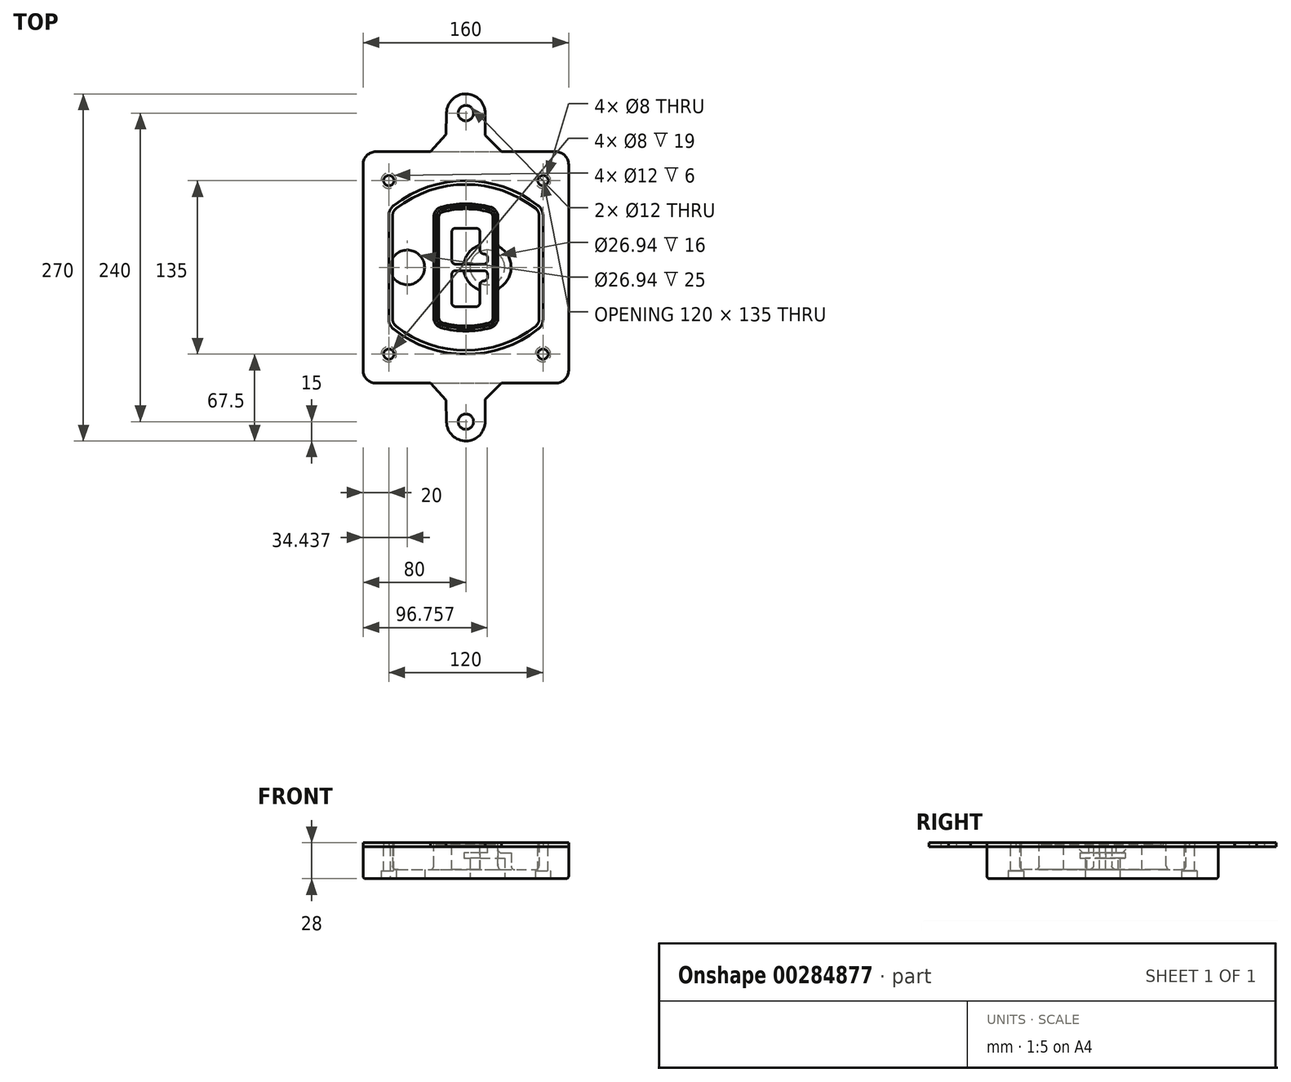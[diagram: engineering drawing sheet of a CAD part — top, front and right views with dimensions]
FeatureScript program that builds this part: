
annotation { "Feature Type Name" : "Feature", "Feature Type Description" : "" }
export const myFeature = defineFeature(function(context is Context, id is Id, definition is map)
    precondition{}
    {
        {
            var Q0;
            Q0=qCreatedBy(makeId("Top.planeOp"),FACE);
            var sketch = newSketch(context, id + "F0", { "sketchPlane" : qUnion([Q0])});
            skPoint(sketch, "E0.rect.middle", {"position": v(0, 0) * mm});
            skLineSegment(sketch, "E1.bottom", {"start": v(-70, -90) * mm, "end": v(70, -90) * mm});
            skLineSegment(sketch, "E1.top", {"start": v(-70, 90) * mm, "end": v(70, 90) * mm});
            skLineSegment(sketch, "E1.left", {"start": v(-80, -80) * mm, "end": v(-80, 80) * mm});
            skLineSegment(sketch, "E1.right", {"start": v(80, -80) * mm, "end": v(80, 80) * mm});
            skLineSegment(sketch, "E2", {"start": v(-80, 90) * mm, "end": v(80, -90) * mm, "construction": true});
            skLineSegment(sketch, "E3", {"start": v(80, 90) * mm, "end": v(-80, -90) * mm, "construction": true});
            skCircle(sketch, "E4", {"center": v(-60, 67.5) * mm, "radius": 4 * mm});
            skCircle(sketch, "E5", {"center": v(60, 67.5) * mm, "radius": 4 * mm});
            skCircle(sketch, "E6", {"center": v(60, -67.5) * mm, "radius": 4 * mm});
            skCircle(sketch, "E7", {"center": v(-60, -67.5) * mm, "radius": 4 * mm});
            skLineSegment(sketch, "E8", {"start": v(-60, 67.5) * mm, "end": v(60, 67.5) * mm, "construction": true});
            skLineSegment(sketch, "E9", {"start": v(60, 67.5) * mm, "end": v(60, -67.5) * mm, "construction": true});
            skLineSegment(sketch, "E10", {"start": v(60, -67.5) * mm, "end": v(-60, -67.5) * mm, "construction": true});
            skLineSegment(sketch, "E11", {"start": v(-60, -67.5) * mm, "end": v(-60, 67.5) * mm, "construction": true});
            skLineSegment(sketch, "E12", {"start": v(-60, 40.3) * mm, "end": v(-60, -40.3) * mm});
            skLineSegment(sketch, "E13", {"start": v(60, 40.3) * mm, "end": v(60, -40.3) * mm});
            skArc(sketch, "E14", {"start": v(56.15, 48.18) * mm, "mid": v(0, 67.5) * mm, "end": v(-56.15, 48.18) * mm});
            skArc(sketch, "E15", {"start": v(-56.15, -48.18) * mm, "mid": v(0, -67.5) * mm, "end": v(56.15, -48.18) * mm});
            skLineSegment(sketch, "E16", {"start": v(-60, 0) * mm, "end": v(60, 0) * mm, "construction": true});
            skPoint(sketch, "E17.visualSharp", {"position": v(-60, -45) * mm});
            skArc(sketch, "E17.filletArc", {"start": v(-60, -40.3) * mm, "mid": v(-58.99, -44.68) * mm, "end": v(-56.15, -48.18) * mm});
            skPoint(sketch, "E18.visualSharp", {"position": v(-60, 45) * mm});
            skArc(sketch, "E18.filletArc", {"start": v(-56.15, 48.18) * mm, "mid": v(-58.99, 44.68) * mm, "end": v(-60, 40.3) * mm});
            skPoint(sketch, "E19.visualSharp", {"position": v(60, 45) * mm});
            skArc(sketch, "E19.filletArc", {"start": v(60, 40.3) * mm, "mid": v(58.99, 44.68) * mm, "end": v(56.15, 48.18) * mm});
            skPoint(sketch, "E20.visualSharp", {"position": v(60, -45) * mm});
            skArc(sketch, "E20.filletArc", {"start": v(56.15, -48.18) * mm, "mid": v(58.99, -44.68) * mm, "end": v(60, -40.3) * mm});
            skPoint(sketch, "E21.visualSharp", {"position": v(-80, 90) * mm});
            skArc(sketch, "E21.filletArc", {"start": v(-70, 90) * mm, "mid": v(-77.07, 87.07) * mm, "end": v(-80, 80) * mm});
            skPoint(sketch, "E22.visualSharp", {"position": v(80, 90) * mm});
            skArc(sketch, "E22.filletArc", {"start": v(80, 80) * mm, "mid": v(77.07, 87.07) * mm, "end": v(70, 90) * mm});
            skPoint(sketch, "E23.visualSharp", {"position": v(80, -90) * mm});
            skArc(sketch, "E23.filletArc", {"start": v(70, -90) * mm, "mid": v(77.07, -87.07) * mm, "end": v(80, -80) * mm});
            skPoint(sketch, "E24.visualSharp", {"position": v(-80, -90) * mm});
            skArc(sketch, "E24.filletArc", {"start": v(-80, -80) * mm, "mid": v(-77.07, -87.07) * mm, "end": v(-70, -90) * mm});
            skArc(sketch, "E25.0", {"start": v(57, 40.3) * mm, "mid": v(56.3, 43.36) * mm, "end": v(54.3, 45.81) * mm});
            skLineSegment(sketch, "E25.1", {"start": v(57, 40.3) * mm, "end": v(57, -40.3) * mm});
            skArc(sketch, "E25.2", {"start": v(54.3, -45.81) * mm, "mid": v(56.3, -43.36) * mm, "end": v(57, -40.3) * mm});
            skArc(sketch, "E25.3", {"start": v(-54.3, -45.81) * mm, "mid": v(0, -64.5) * mm, "end": v(54.3, -45.81) * mm});
            skArc(sketch, "E25.4", {"start": v(-57, -40.3) * mm, "mid": v(-56.3, -43.36) * mm, "end": v(-54.3, -45.81) * mm});
            skArc(sketch, "E25.5", {"start": v(54.3, 45.81) * mm, "mid": v(0, 64.5) * mm, "end": v(-54.3, 45.81) * mm});
            skLineSegment(sketch, "E25.6", {"start": v(-57, 40.3) * mm, "end": v(-57, -40.3) * mm});
            skArc(sketch, "E25.7", {"start": v(-54.3, 45.81) * mm, "mid": v(-56.3, 43.36) * mm, "end": v(-57, 40.3) * mm});
            skArc(sketch, "E26.0", {"start": v(-58.62, 51.33) * mm, "mid": v(-62.58, 46.43) * mm, "end": v(-64, 40.3) * mm});
            skArc(sketch, "E26.1", {"start": v(58.62, 51.33) * mm, "mid": v(0, 71.5) * mm, "end": v(-58.62, 51.33) * mm});
            skArc(sketch, "E26.2", {"start": v(64, 40.3) * mm, "mid": v(62.58, 46.43) * mm, "end": v(58.62, 51.33) * mm});
            skLineSegment(sketch, "E26.3", {"start": v(64, 40.3) * mm, "end": v(64, -40.3) * mm});
            skArc(sketch, "E26.4", {"start": v(58.62, -51.33) * mm, "mid": v(62.58, -46.43) * mm, "end": v(64, -40.3) * mm});
            skLineSegment(sketch, "E26.5", {"start": v(-64, 40.3) * mm, "end": v(-64, -40.3) * mm});
            skArc(sketch, "E26.6", {"start": v(-58.62, -51.33) * mm, "mid": v(0, -71.5) * mm, "end": v(58.62, -51.33) * mm});
            skArc(sketch, "E26.7", {"start": v(-64, -40.3) * mm, "mid": v(-62.58, -46.43) * mm, "end": v(-58.62, -51.33) * mm});
            skSolve(sketch);
        }
        {
            var Q0;
            Q0=makeQuery(id+"F0.imprint","IMPRINT",FACE,{"disambiguationData":[TD([[makeQuery(id+"F0.imprint","IMPRINT",EDGE,{"derivedFrom":sQuery(id+"F0.wireOp",EDGE,"E1.bottom")}),1.0]])]});
            var Q1;
            Q1=makeQuery(id+"F0.imprint","IMPRINT",FACE,{"disambiguationData":[TD([[makeQuery(id+"F0.imprint","IMPRINT",EDGE,{"derivedFrom":sQuery(id+"F0.wireOp",EDGE,"E12")}),1.0]])]});
            var Q2;
            Q2=makeQuery(id+"F0.imprint","IMPRINT",FACE,{"disambiguationData":[TD([[makeQuery(id+"F0.imprint","IMPRINT",EDGE,{"derivedFrom":sQuery(id+"F0.wireOp",EDGE,"E25.0")}),1.0]])]});
            var Q3;
            Q3=makeQuery(id+"F0.imprint","IMPRINT",FACE,{"disambiguationData":[TD([[makeQuery(id+"F0.imprint","IMPRINT",EDGE,{"derivedFrom":sQuery(id+"F0.wireOp",EDGE,"E12")}),-1.0]])]});
            extrude(context, id + "F1", {"entities" : qUnion([Q0, Q1, Q2, Q3]), "oppositeDirection" : true, "depth" : 25 * mm});
        }
        {
            var Q0;
            Q0=makeQuery(id+"F0.imprint","IMPRINT",FACE,{"disambiguationData":[TD([[makeQuery(id+"F0.imprint","IMPRINT",EDGE,{"derivedFrom":sQuery(id+"F0.wireOp",EDGE,"E12")}),1.0]])]});
            extrude(context, id + "F2", {"entities" : qUnion([Q0]), "operationType" : NewBodyOperationType.ADD, "depth" : 3 * mm});
        }
        {
            var Q0;
            Q0=makeQuery(id+"F0.imprint","IMPRINT",FACE,{"disambiguationData":[TD([[makeQuery(id+"F0.imprint","IMPRINT",EDGE,{"derivedFrom":sQuery(id+"F0.wireOp",EDGE,"E25.0")}),1.0]])]});
            extrude(context, id + "F3", {"entities" : qUnion([Q0]), "operationType" : NewBodyOperationType.REMOVE, "oppositeDirection" : true, "depth" : 18 * mm});
        }
        {
            var Q0;
            Q0=makeQuery(id+"F2.opExtrude","CAP_FACE",FACE,{"disambiguationData":[OSD([sQuery(id+"F0.wireOp",EDGE,"E12"),sQuery(id+"F0.wireOp",EDGE,"E13"),sQuery(id+"F0.wireOp",EDGE,"E14"),sQuery(id+"F0.wireOp",EDGE,"E15"),sQuery(id+"F0.wireOp",EDGE,"E17.filletArc"),sQuery(id+"F0.wireOp",EDGE,"E18.filletArc"),sQuery(id+"F0.wireOp",EDGE,"E19.filletArc"),sQuery(id+"F0.wireOp",EDGE,"E20.filletArc"),sQuery(id+"F0.wireOp",EDGE,"E25.0"),sQuery(id+"F0.wireOp",EDGE,"E25.1"),sQuery(id+"F0.wireOp",EDGE,"E25.2"),sQuery(id+"F0.wireOp",EDGE,"E25.3"),sQuery(id+"F0.wireOp",EDGE,"E25.4"),sQuery(id+"F0.wireOp",EDGE,"E25.5"),sQuery(id+"F0.wireOp",EDGE,"E25.6"),sQuery(id+"F0.wireOp",EDGE,"E25.7")])],"isStart":false});
            var sketch = newSketch(context, id + "F4", { "sketchPlane" : qUnion([Q0])});
            skArc(sketch, "E27.0", {"start": v(-19.08, -46.97) * mm, "mid": v(0, -49.5) * mm, "end": v(19.08, -46.97) * mm});
            skArc(sketch, "E28.0", {"start": v(19.08, 46.97) * mm, "mid": v(0, 49.5) * mm, "end": v(-19.08, 46.97) * mm});
            skLineSegment(sketch, "E29", {"start": v(-25, 39.25) * mm, "end": v(-25, -39.25) * mm});
            skLineSegment(sketch, "E30", {"start": v(25, 39.25) * mm, "end": v(25, -39.25) * mm});
            skLineSegment(sketch, "E31", {"start": v(-25, 45.1) * mm, "end": v(25, 45.1) * mm, "construction": true});
            skLineSegment(sketch, "E32", {"start": v(-25, -45.1) * mm, "end": v(25, -45.1) * mm, "construction": true});
            skPoint(sketch, "E33.visualSharp", {"position": v(-25, 45.1) * mm});
            skArc(sketch, "E33.filletArc", {"start": v(-19.08, 46.97) * mm, "mid": v(-23.35, 44.11) * mm, "end": v(-25, 39.25) * mm});
            skPoint(sketch, "E34.visualSharp", {"position": v(25, 45.1) * mm});
            skArc(sketch, "E34.filletArc", {"start": v(25, 39.25) * mm, "mid": v(23.35, 44.11) * mm, "end": v(19.08, 46.97) * mm});
            skPoint(sketch, "E35.visualSharp", {"position": v(25, -45.1) * mm});
            skArc(sketch, "E35.filletArc", {"start": v(19.08, -46.97) * mm, "mid": v(23.35, -44.11) * mm, "end": v(25, -39.25) * mm});
            skPoint(sketch, "E36.visualSharp", {"position": v(-25, -45.1) * mm});
            skArc(sketch, "E36.filletArc", {"start": v(-25, -39.25) * mm, "mid": v(-23.35, -44.11) * mm, "end": v(-19.08, -46.97) * mm});
            skArc(sketch, "E37.0", {"start": v(54.3, 45.81) * mm, "mid": v(0, 64.5) * mm, "end": v(-54.3, 45.81) * mm});
            skArc(sketch, "E37.1", {"start": v(-54.3, 45.81) * mm, "mid": v(-56.3, 43.36) * mm, "end": v(-57, 40.3) * mm});
            skLineSegment(sketch, "E37.2", {"start": v(-57, 40.3) * mm, "end": v(-57, -40.3) * mm});
            skArc(sketch, "E37.3", {"start": v(-57, -40.3) * mm, "mid": v(-56.3, -43.36) * mm, "end": v(-54.3, -45.81) * mm});
            skArc(sketch, "E37.4", {"start": v(-54.3, -45.81) * mm, "mid": v(0, -64.5) * mm, "end": v(54.3, -45.81) * mm});
            skArc(sketch, "E37.5", {"start": v(54.3, -45.81) * mm, "mid": v(56.3, -43.36) * mm, "end": v(57, -40.3) * mm});
            skLineSegment(sketch, "E37.6", {"start": v(57, 40.3) * mm, "end": v(57, -40.3) * mm});
            skArc(sketch, "E37.7", {"start": v(57, 40.3) * mm, "mid": v(56.3, 43.36) * mm, "end": v(54.3, 45.81) * mm});
            skLineSegment(sketch, "E38.0", {"start": v(23, 39.25) * mm, "end": v(23, -39.25) * mm});
            skArc(sketch, "E38.1", {"start": v(18.56, -45.04) * mm, "mid": v(21.76, -42.9) * mm, "end": v(23, -39.25) * mm});
            skArc(sketch, "E38.2", {"start": v(-18.56, -45.04) * mm, "mid": v(0, -47.5) * mm, "end": v(18.56, -45.04) * mm});
            skArc(sketch, "E38.3", {"start": v(-23, -39.25) * mm, "mid": v(-21.76, -42.9) * mm, "end": v(-18.56, -45.04) * mm});
            skLineSegment(sketch, "E38.4", {"start": v(-23, 39.25) * mm, "end": v(-23, -39.25) * mm});
            skArc(sketch, "E38.5", {"start": v(23, 39.25) * mm, "mid": v(21.76, 42.9) * mm, "end": v(18.56, 45.04) * mm});
            skArc(sketch, "E38.6", {"start": v(-18.56, 45.04) * mm, "mid": v(-21.76, 42.9) * mm, "end": v(-23, 39.25) * mm});
            skArc(sketch, "E38.7", {"start": v(18.56, 45.04) * mm, "mid": v(0, 47.5) * mm, "end": v(-18.56, 45.04) * mm});
            skArc(sketch, "E39.0", {"start": v(21, 39.25) * mm, "mid": v(20.18, 41.68) * mm, "end": v(18.04, 43.1) * mm});
            skLineSegment(sketch, "E39.1", {"start": v(21, 39.25) * mm, "end": v(21, -39.25) * mm});
            skArc(sketch, "E39.2", {"start": v(18.04, -43.1) * mm, "mid": v(20.18, -41.68) * mm, "end": v(21, -39.25) * mm});
            skArc(sketch, "E39.3", {"start": v(-18.04, -43.1) * mm, "mid": v(0, -45.5) * mm, "end": v(18.04, -43.1) * mm});
            skArc(sketch, "E39.4", {"start": v(-21, -39.25) * mm, "mid": v(-20.18, -41.68) * mm, "end": v(-18.04, -43.1) * mm});
            skArc(sketch, "E39.5", {"start": v(18.04, 43.1) * mm, "mid": v(0, 45.5) * mm, "end": v(-18.04, 43.1) * mm});
            skLineSegment(sketch, "E39.6", {"start": v(-21, 39.25) * mm, "end": v(-21, -39.25) * mm});
            skArc(sketch, "E39.7", {"start": v(-18.04, 43.1) * mm, "mid": v(-20.18, 41.68) * mm, "end": v(-21, 39.25) * mm});
            skLineSegment(sketch, "E40", {"start": v(-25, 0) * mm, "end": v(25, 0) * mm, "construction": true});
            skLineSegment(sketch, "E41", {"start": v(-11, 5.5) * mm, "end": v(-11, 27.5) * mm});
            skLineSegment(sketch, "E42", {"start": v(-8, 30.5) * mm, "end": v(8, 30.5) * mm});
            skLineSegment(sketch, "E43", {"start": v(11, 27.5) * mm, "end": v(11, 13.5) * mm});
            skLineSegment(sketch, "E44", {"start": v(14, 10.5) * mm, "end": v(14, 10.5) * mm});
            skLineSegment(sketch, "E45", {"start": v(17, 7.5) * mm, "end": v(17, 5.5) * mm});
            skLineSegment(sketch, "E46", {"start": v(14, 2.5) * mm, "end": v(-8, 2.5) * mm});
            skPoint(sketch, "E47.visualSharp", {"position": v(-11, 30.5) * mm});
            skArc(sketch, "E47.filletArc", {"start": v(-8, 30.5) * mm, "mid": v(-10.12, 29.62) * mm, "end": v(-11, 27.5) * mm});
            skPoint(sketch, "E48.visualSharp", {"position": v(11, 30.5) * mm});
            skArc(sketch, "E48.filletArc", {"start": v(11, 27.5) * mm, "mid": v(10.12, 29.62) * mm, "end": v(8, 30.5) * mm});
            skPoint(sketch, "E49.visualSharp", {"position": v(11, 10.5) * mm});
            skArc(sketch, "E49.filletArc", {"start": v(11, 13.5) * mm, "mid": v(11.88, 11.38) * mm, "end": v(14, 10.5) * mm});
            skPoint(sketch, "E50.visualSharp", {"position": v(17, 10.5) * mm});
            skArc(sketch, "E50.filletArc", {"start": v(17, 7.5) * mm, "mid": v(16.12, 9.62) * mm, "end": v(14, 10.5) * mm});
            skPoint(sketch, "E51.visualSharp", {"position": v(17, 2.5) * mm});
            skArc(sketch, "E51.filletArc", {"start": v(14, 2.5) * mm, "mid": v(16.12, 3.38) * mm, "end": v(17, 5.5) * mm});
            skPoint(sketch, "E52.visualSharp", {"position": v(-11, 2.5) * mm});
            skArc(sketch, "E52.filletArc", {"start": v(-11, 5.5) * mm, "mid": v(-10.12, 3.38) * mm, "end": v(-8, 2.5) * mm});
            skLineSegment(sketch, "E53.0.MirrorCS", {"start": v(14, -2.5) * mm, "end": v(-8, -2.5) * mm});
            skArc(sketch, "E54.0.MirrorCS", {"start": v(-11, -5.5) * mm, "mid": v(-10.12, -3.38) * mm, "end": v(-8, -2.5) * mm});
            skLineSegment(sketch, "E55.0.MirrorCS", {"start": v(-11, -5.5) * mm, "end": v(-11, -27.5) * mm});
            skArc(sketch, "E56.0.MirrorCS", {"start": v(-8, -30.5) * mm, "mid": v(-10.12, -29.62) * mm, "end": v(-11, -27.5) * mm});
            skLineSegment(sketch, "E57.0.MirrorCS", {"start": v(-8, -30.5) * mm, "end": v(8, -30.5) * mm});
            skArc(sketch, "E58.0.MirrorCS", {"start": v(11, -27.5) * mm, "mid": v(10.12, -29.62) * mm, "end": v(8, -30.5) * mm});
            skLineSegment(sketch, "E59.0.MirrorCS", {"start": v(11, -27.5) * mm, "end": v(11, -13.5) * mm});
            skArc(sketch, "E60.0.MirrorCS", {"start": v(11, -13.5) * mm, "mid": v(11.88, -11.38) * mm, "end": v(14, -10.5) * mm});
            skArc(sketch, "E61.0.MirrorCS", {"start": v(17, -7.5) * mm, "mid": v(16.12, -9.62) * mm, "end": v(14, -10.5) * mm});
            skLineSegment(sketch, "E62.0.MirrorCS", {"start": v(17, -7.5) * mm, "end": v(17, -5.5) * mm});
            skArc(sketch, "E63.0.MirrorCS", {"start": v(14, -2.5) * mm, "mid": v(16.12, -3.38) * mm, "end": v(17, -5.5) * mm});
            skSolve(sketch);
        }
        {
            var Q0;
            Q0=makeQuery(id+"F4.imprint","IMPRINT",FACE,{"disambiguationData":[TD([[makeQuery(id+"F4.imprint","IMPRINT",EDGE,{"derivedFrom":sQuery(id+"F4.wireOp",EDGE,"E27.0")}),1.0]])]});
            var Q1;
            Q1=makeQuery(id+"F4.imprint","IMPRINT",FACE,{"disambiguationData":[TD([[makeQuery(id+"F4.imprint","IMPRINT",EDGE,{"derivedFrom":sQuery(id+"F4.wireOp",EDGE,"E38.0")}),-1.0]])]});
            var Q2;
            Q2=makeQuery(id+"F4.imprint","IMPRINT",FACE,{"disambiguationData":[TD([[makeQuery(id+"F4.imprint","IMPRINT",EDGE,{"derivedFrom":sQuery(id+"F4.wireOp",EDGE,"E39.0")}),1.0]])]});
            extrude(context, id + "F5", {"entities" : qUnion([Q0, Q1, Q2]), "operationType" : NewBodyOperationType.ADD, "endBound" : BoundingType.UP_TO_NEXT, "oppositeDirection" : true, "depth" : 25 * mm});
        }
        {
            var Q0;
            Q0=makeQuery(id+"F4.imprint","IMPRINT",FACE,{"disambiguationData":[TD([[makeQuery(id+"F4.imprint","IMPRINT",EDGE,{"derivedFrom":sQuery(id+"F4.wireOp",EDGE,"E38.0")}),-1.0]])]});
            extrude(context, id + "F6", {"entities" : qUnion([Q0]), "operationType" : NewBodyOperationType.REMOVE, "oppositeDirection" : true, "depth" : 2 * mm});
        }
        {
            var Q0;
            Q0=makeQuery(id+"F1.opExtrude","CAP_FACE",FACE,{"disambiguationData":[OSD([sQuery(id+"F0.wireOp",EDGE,"E1.bottom"),sQuery(id+"F0.wireOp",EDGE,"E1.top"),sQuery(id+"F0.wireOp",EDGE,"E1.left"),sQuery(id+"F0.wireOp",EDGE,"E1.right"),sQuery(id+"F0.wireOp",EDGE,"E4"),sQuery(id+"F0.wireOp",EDGE,"E5"),sQuery(id+"F0.wireOp",EDGE,"E6"),sQuery(id+"F0.wireOp",EDGE,"E7"),sQuery(id+"F0.wireOp",EDGE,"E21.filletArc"),sQuery(id+"F0.wireOp",EDGE,"E22.filletArc"),sQuery(id+"F0.wireOp",EDGE,"E23.filletArc"),sQuery(id+"F0.wireOp",EDGE,"E24.filletArc")])],"isStart":false});
            var sketch = newSketch(context, id + "F7", { "sketchPlane" : qUnion([Q0])});
            skCircle(sketch, "E64", {"center": v(16.76, 0) * mm, "radius": 13.47 * mm});
            skCircle(sketch, "E65", {"center": v(-45.56, 0) * mm, "radius": 13.47 * mm});
            skLineSegment(sketch, "E66", {"start": v(80, 0) * mm, "end": v(-80, 0) * mm});
            skCircle(sketch, "E67", {"center": v(16.76, 0) * mm, "radius": 18.47 * mm});
            skCircle(sketch, "E68", {"center": v(60, -67.5) * mm, "radius": 6 * mm});
            skCircle(sketch, "E69", {"center": v(-60, -67.5) * mm, "radius": 6 * mm});
            skCircle(sketch, "E70", {"center": v(-60, 67.5) * mm, "radius": 6 * mm});
            skCircle(sketch, "E71", {"center": v(60, 67.5) * mm, "radius": 6 * mm});
            skSolve(sketch);
        }
        {
            var Q0;
            {var subQ1=sQuery(id+"F7.wireOp",EDGE,"E66");var subQ4=sQuery(id+"F7.wireOp",EDGE,"E64");var subQ6=makeQuery(id+"F7.imprint","INTERSECT",VERTEX,{"disambiguationData":[OD(0.0)],"derivedFrom":[subQ4,subQ1]});Q0=makeQuery(id+"F7.imprint","IMPRINT",FACE,{"disambiguationData":[TD([[makeQuery(id+"F7.imprint","IMPRINT",EDGE,{"disambiguationData":[TD([[subQ6,-1.0]])],"derivedFrom":subQ4}),-1.0]])]});}
            var Q1;
            {var subQ0=sQuery(id+"F7.wireOp",EDGE,"E66");var subQ1=sQuery(id+"F7.wireOp",EDGE,"E64");var subQ3=makeQuery(id+"F7.imprint","INTERSECT",VERTEX,{"disambiguationData":[OD(0.0)],"derivedFrom":[subQ1,subQ0]});Q1=makeQuery(id+"F7.imprint","IMPRINT",FACE,{"disambiguationData":[TD([[makeQuery(id+"F7.imprint","IMPRINT",EDGE,{"disambiguationData":[TD([[subQ3,-1.0]])],"derivedFrom":subQ1}),1.0]])]});}
            var Q2;
            {var subQ0=sQuery(id+"F7.wireOp",EDGE,"E66");var subQ1=sQuery(id+"F7.wireOp",EDGE,"E64");var subQ3=makeQuery(id+"F7.imprint","INTERSECT",VERTEX,{"disambiguationData":[OD(0.0)],"derivedFrom":[subQ1,subQ0]});Q2=makeQuery(id+"F7.imprint","IMPRINT",FACE,{"disambiguationData":[TD([[makeQuery(id+"F7.imprint","IMPRINT",EDGE,{"disambiguationData":[TD([[subQ3,1.0]])],"derivedFrom":subQ1}),1.0]])]});}
            var Q3;
            {var subQ1=sQuery(id+"F7.wireOp",EDGE,"E66");var subQ4=sQuery(id+"F7.wireOp",EDGE,"E64");var subQ6=makeQuery(id+"F7.imprint","INTERSECT",VERTEX,{"disambiguationData":[OD(0.0)],"derivedFrom":[subQ4,subQ1]});Q3=makeQuery(id+"F7.imprint","IMPRINT",FACE,{"disambiguationData":[TD([[makeQuery(id+"F7.imprint","IMPRINT",EDGE,{"disambiguationData":[TD([[subQ6,1.0]])],"derivedFrom":subQ4}),-1.0]])]});}
            extrude(context, id + "F8", {"entities" : qUnion([Q0, Q1, Q2, Q3]), "operationType" : NewBodyOperationType.ADD, "oppositeDirection" : true, "depth" : 20 * mm});
        }
        {
            var Q0;
            {var subQ0=sQuery(id+"F7.wireOp",EDGE,"E66");var subQ1=sQuery(id+"F7.wireOp",EDGE,"E64");var subQ3=makeQuery(id+"F7.imprint","INTERSECT",VERTEX,{"disambiguationData":[OD(0.0)],"derivedFrom":[subQ1,subQ0]});Q0=makeQuery(id+"F7.imprint","IMPRINT",FACE,{"disambiguationData":[TD([[makeQuery(id+"F7.imprint","IMPRINT",EDGE,{"disambiguationData":[TD([[subQ3,-1.0]])],"derivedFrom":subQ1}),1.0]])]});}
            var Q1;
            {var subQ0=sQuery(id+"F7.wireOp",EDGE,"E66");var subQ1=sQuery(id+"F7.wireOp",EDGE,"E64");var subQ3=makeQuery(id+"F7.imprint","INTERSECT",VERTEX,{"disambiguationData":[OD(0.0)],"derivedFrom":[subQ1,subQ0]});Q1=makeQuery(id+"F7.imprint","IMPRINT",FACE,{"disambiguationData":[TD([[makeQuery(id+"F7.imprint","IMPRINT",EDGE,{"disambiguationData":[TD([[subQ3,1.0]])],"derivedFrom":subQ1}),1.0]])]});}
            extrude(context, id + "F9", {"entities" : qUnion([Q0, Q1]), "operationType" : NewBodyOperationType.REMOVE, "oppositeDirection" : true, "depth" : 16 * mm});
        }
        {
            var Q0;
            {var subQ0=sQuery(id+"F7.wireOp",EDGE,"E66");var subQ1=sQuery(id+"F7.wireOp",EDGE,"E65");var subQ3=makeQuery(id+"F7.imprint","INTERSECT",VERTEX,{"disambiguationData":[OD(0.0)],"derivedFrom":[subQ1,subQ0]});Q0=makeQuery(id+"F7.imprint","IMPRINT",FACE,{"disambiguationData":[TD([[makeQuery(id+"F7.imprint","IMPRINT",EDGE,{"disambiguationData":[TD([[subQ3,-1.0]])],"derivedFrom":subQ1}),1.0]])]});}
            var Q1;
            {var subQ0=sQuery(id+"F7.wireOp",EDGE,"E66");var subQ1=sQuery(id+"F7.wireOp",EDGE,"E65");var subQ3=makeQuery(id+"F7.imprint","INTERSECT",VERTEX,{"disambiguationData":[OD(0.0)],"derivedFrom":[subQ1,subQ0]});Q1=makeQuery(id+"F7.imprint","IMPRINT",FACE,{"disambiguationData":[TD([[makeQuery(id+"F7.imprint","IMPRINT",EDGE,{"disambiguationData":[TD([[subQ3,1.0]])],"derivedFrom":subQ1}),1.0]])]});}
            extrude(context, id + "F10", {"entities" : qUnion([Q0, Q1]), "operationType" : NewBodyOperationType.REMOVE, "oppositeDirection" : true, "depth" : 25 * mm});
        }
        {
            var Q0;
            Q0=makeQuery(id+"F7.imprint","IMPRINT",FACE,{"disambiguationData":[TD([[makeQuery(id+"F7.imprint","IMPRINT",EDGE,{"derivedFrom":sQuery(id+"F7.wireOp",EDGE,"E68")}),1.0]])]});
            var Q1;
            Q1=makeQuery(id+"F7.imprint","IMPRINT",FACE,{"disambiguationData":[TD([[makeQuery(id+"F7.imprint","IMPRINT",EDGE,{"derivedFrom":makeQuery(id+"F1.opExtrude","CAP_EDGE",EDGE,{"disambiguationData":[OSD([sQuery(id+"F0.wireOp",EDGE,"E5")])],"isStart":false})}),-1.0]])]});
            var Q2;
            Q2=makeQuery(id+"F7.imprint","IMPRINT",FACE,{"disambiguationData":[TD([[makeQuery(id+"F7.imprint","IMPRINT",EDGE,{"derivedFrom":sQuery(id+"F7.wireOp",EDGE,"E69")}),1.0]])]});
            var Q3;
            Q3=makeQuery(id+"F7.imprint","IMPRINT",FACE,{"disambiguationData":[TD([[makeQuery(id+"F7.imprint","IMPRINT",EDGE,{"derivedFrom":makeQuery(id+"F1.opExtrude","CAP_EDGE",EDGE,{"disambiguationData":[OSD([sQuery(id+"F0.wireOp",EDGE,"E4")])],"isStart":false})}),-1.0]])]});
            var Q4;
            Q4=makeQuery(id+"F7.imprint","IMPRINT",FACE,{"disambiguationData":[TD([[makeQuery(id+"F7.imprint","IMPRINT",EDGE,{"derivedFrom":sQuery(id+"F7.wireOp",EDGE,"E70")}),1.0]])]});
            var Q5;
            Q5=makeQuery(id+"F7.imprint","IMPRINT",FACE,{"disambiguationData":[TD([[makeQuery(id+"F7.imprint","IMPRINT",EDGE,{"derivedFrom":makeQuery(id+"F1.opExtrude","CAP_EDGE",EDGE,{"disambiguationData":[OSD([sQuery(id+"F0.wireOp",EDGE,"E7")])],"isStart":false})}),-1.0]])]});
            var Q6;
            Q6=makeQuery(id+"F7.imprint","IMPRINT",FACE,{"disambiguationData":[TD([[makeQuery(id+"F7.imprint","IMPRINT",EDGE,{"derivedFrom":sQuery(id+"F7.wireOp",EDGE,"E71")}),1.0]])]});
            var Q7;
            Q7=makeQuery(id+"F7.imprint","IMPRINT",FACE,{"disambiguationData":[TD([[makeQuery(id+"F7.imprint","IMPRINT",EDGE,{"derivedFrom":makeQuery(id+"F1.opExtrude","CAP_EDGE",EDGE,{"disambiguationData":[OSD([sQuery(id+"F0.wireOp",EDGE,"E6")])],"isStart":false})}),-1.0]])]});
            extrude(context, id + "F11", {"entities" : qUnion([Q0, Q1, Q2, Q3, Q4, Q5, Q6, Q7]), "operationType" : NewBodyOperationType.REMOVE, "oppositeDirection" : true, "depth" : 6 * mm});
        }
        {
            var Q0;
            Q0=makeQuery(id+"F9.boolean.opBoolean","COPY",FACE,{"derivedFrom":makeQuery(id+"F9.opExtrude","CAP_FACE",FACE,{"disambiguationData":[OSD([sQuery(id+"F7.wireOp",EDGE,"E64")])],"isStart":false})});
            var sketch = newSketch(context, id + "F12", { "sketchPlane" : qUnion([Q0])});
            skArc(sketch, "E72.0", {"start": v(11, 17.55) * mm, "mid": v(2.57, 11.82) * mm, "end": v(-1.54, 2.5) * mm});
            skArc(sketch, "E72.1", {"start": v(-1.54, -2.5) * mm, "mid": v(2.57, -11.82) * mm, "end": v(11, -17.55) * mm});
            skLineSegment(sketch, "E73", {"start": v(-1.54, -2.5) * mm, "end": v(14, -2.5) * mm});
            skLineSegment(sketch, "E74.0", {"start": v(14, 2.5) * mm, "end": v(-1.54, 2.5) * mm});
            skArc(sketch, "E74.1", {"start": v(14, 2.5) * mm, "mid": v(16.12, 3.38) * mm, "end": v(17, 5.5) * mm});
            skLineSegment(sketch, "E74.2", {"start": v(17, 7.5) * mm, "end": v(17, 5.5) * mm});
            skArc(sketch, "E74.3", {"start": v(17, 7.5) * mm, "mid": v(16.12, 9.62) * mm, "end": v(14, 10.5) * mm});
            skArc(sketch, "E74.4", {"start": v(11, 13.5) * mm, "mid": v(11.88, 11.38) * mm, "end": v(14, 10.5) * mm});
            skLineSegment(sketch, "E74.5", {"start": v(11, 17.55) * mm, "end": v(11, 13.5) * mm});
            skLineSegment(sketch, "E74.7", {"start": v(14, -2.5) * mm, "end": v(-1.54, -2.5) * mm});
            skArc(sketch, "E74.8", {"start": v(14, -2.5) * mm, "mid": v(16.12, -3.38) * mm, "end": v(17, -5.5) * mm});
            skLineSegment(sketch, "E74.9", {"start": v(17, -7.5) * mm, "end": v(17, -5.5) * mm});
            skArc(sketch, "E74.10", {"start": v(17, -7.5) * mm, "mid": v(16.12, -9.62) * mm, "end": v(14, -10.5) * mm});
            skArc(sketch, "E74.11", {"start": v(11, -13.5) * mm, "mid": v(11.88, -11.38) * mm, "end": v(14, -10.5) * mm});
            skLineSegment(sketch, "E74.12", {"start": v(11, -17.55) * mm, "end": v(11, -13.5) * mm});
            skPoint(sketch, "E75.orphan", {"position": v(11, -27.5) * mm});
            skPoint(sketch, "E76.orphan", {"position": v(-8, -2.5) * mm});
            skPoint(sketch, "E77.orphan", {"position": v(-8, 2.5) * mm});
            skPoint(sketch, "E78.orphan", {"position": v(11, 27.5) * mm});
            skSolve(sketch);
        }
        {
            var Q0;
            {var subQ7=sQuery(id+"F12.wireOp",EDGE,"E72.0");var subQ14=sQuery(id+"F12.wireOp",EDGE,"E72.1");var subQ16=sQuery(id+"F12.wireOp",EDGE,"E74.1");var subQ18=sQuery(id+"F12.wireOp",EDGE,"E74.8");Q0=qUnion([makeQuery(id+"F12.imprint","IMPRINT",FACE,{"disambiguationData":[TD([[makeQuery(id+"F12.imprint","IMPRINT",EDGE,{"derivedFrom":subQ7}),1.0]])]}),makeQuery(id+"F12.imprint","IMPRINT",FACE,{"disambiguationData":[TD([[makeQuery(id+"F12.imprint","IMPRINT",EDGE,{"derivedFrom":subQ14}),1.0]])]}),makeQuery(id+"F12.imprint","IMPRINT",FACE,{"disambiguationData":[TD([[makeQuery(id+"F12.imprint","IMPRINT",EDGE,{"derivedFrom":subQ16}),1.0]])]}),makeQuery(id+"F12.imprint","IMPRINT",FACE,{"disambiguationData":[TD([[makeQuery(id+"F12.imprint","IMPRINT",EDGE,{"derivedFrom":subQ18}),-1.0]])]})]);}
            var Q1;
            Q1=makeQuery(id+"F5.boolean.opBoolean","SPLIT",FACE,{"disambiguationData":[TD([makeQuery(id+"F5.opExtrude","SWEPT_FACE",FACE,{"disambiguationData":[OSD([sQuery(id+"F4.wireOp",EDGE,"E41")])]})])],"derivedFrom":makeQuery(id+"F3.boolean.opBoolean","COPY",FACE,{"derivedFrom":makeQuery(id+"F3.opExtrude","CAP_FACE",FACE,{"disambiguationData":[OSD([sQuery(id+"F0.wireOp",EDGE,"E25.0"),sQuery(id+"F0.wireOp",EDGE,"E25.1"),sQuery(id+"F0.wireOp",EDGE,"E25.2"),sQuery(id+"F0.wireOp",EDGE,"E25.3"),sQuery(id+"F0.wireOp",EDGE,"E25.4"),sQuery(id+"F0.wireOp",EDGE,"E25.5"),sQuery(id+"F0.wireOp",EDGE,"E25.6"),sQuery(id+"F0.wireOp",EDGE,"E25.7")])],"isStart":false})})});
            extrude(context, id + "F13", {"entities" : qUnion([Q0]), "operationType" : NewBodyOperationType.REMOVE, "endBound" : BoundingType.UP_TO_SURFACE, "endBoundEntityFace" : qUnion([Q1]), "depth" : 25 * mm});
        }
        {
            var Q0;
            Q0=makeQuery(id+"F3.boolean.opBoolean","COPY",EDGE,{"derivedFrom":makeQuery(id+"F3.opExtrude","CAP_EDGE",EDGE,{"disambiguationData":[OSD([sQuery(id+"F0.wireOp",EDGE,"E25.6")])],"isStart":false})});
            var Q1;
            Q1=makeQuery(id+"F8.boolean.opBoolean","INTERSECT",EDGE,{"derivedFrom":[makeQuery(id+"F5.opExtrude","SWEPT_FACE",FACE,{"disambiguationData":[OSD([sQuery(id+"F4.wireOp",EDGE,"E30")])]}),makeQuery(id+"F8.opExtrude","CAP_FACE",FACE,{"disambiguationData":[OSD([sQuery(id+"F7.wireOp",EDGE,"E67")])],"isStart":false})]});
            var Q2;
            Q2=makeQuery(id+"F8.boolean.opBoolean","INTERSECT",EDGE,{"disambiguationData":[OD(1.0)],"derivedFrom":[makeQuery(id+"F5.opExtrude","SWEPT_FACE",FACE,{"disambiguationData":[OSD([sQuery(id+"F4.wireOp",EDGE,"E30")])]}),makeQuery(id+"F8.opExtrude","SWEPT_FACE",FACE,{"disambiguationData":[OSD([sQuery(id+"F7.wireOp",EDGE,"E67")])]})]});
            var Q3;
            {var subQ0=sQuery(id+"F4.wireOp",EDGE,"E30");Q3=makeQuery(id+"F8.boolean.opBoolean","SPLIT",EDGE,{"disambiguationData":[TD([makeQuery(id+"F5.opExtrude","SWEPT_FACE",FACE,{"disambiguationData":[OSD([sQuery(id+"F4.wireOp",EDGE,"E35.filletArc")])]})])],"derivedFrom":makeQuery(id+"F5.opExtrude","CAP_EDGE",EDGE,{"disambiguationData":[OSD([subQ0])],"isStart":false})});}
            var Q4;
            {var subQ0=sQuery(id+"F0.wireOp",EDGE,"E25.7");var subQ1=sQuery(id+"F0.wireOp",EDGE,"E25.1");var subQ2=sQuery(id+"F0.wireOp",EDGE,"E25.6");var subQ3=sQuery(id+"F0.wireOp",EDGE,"E25.5");var subQ4=sQuery(id+"F0.wireOp",EDGE,"E25.4");var subQ5=sQuery(id+"F0.wireOp",EDGE,"E25.0");var subQ6=sQuery(id+"F0.wireOp",EDGE,"E25.2");var subQ7=sQuery(id+"F0.wireOp",EDGE,"E25.3");Q4=makeQuery(id+"F8.boolean.opBoolean","INTERSECT",EDGE,{"derivedFrom":[makeQuery(id+"F5.boolean.opBoolean","SPLIT",FACE,{"disambiguationData":[TD([makeQuery(id+"F2.opExtrude","SWEPT_FACE",FACE,{"disambiguationData":[OSD([subQ5])]})])],"derivedFrom":makeQuery(id+"F3.boolean.opBoolean","COPY",FACE,{"derivedFrom":makeQuery(id+"F3.opExtrude","CAP_FACE",FACE,{"disambiguationData":[OSD([subQ5,subQ1,subQ6,subQ7,subQ4,subQ3,subQ2,subQ0])],"isStart":false})})}),makeQuery(id+"F8.opExtrude","SWEPT_FACE",FACE,{"disambiguationData":[OSD([sQuery(id+"F7.wireOp",EDGE,"E67")])]})]});}
            var Q5;
            Q5=makeQuery(id+"F8.boolean.opBoolean","INTERSECT",EDGE,{"disambiguationData":[OD(0.0)],"derivedFrom":[makeQuery(id+"F5.opExtrude","SWEPT_FACE",FACE,{"disambiguationData":[OSD([sQuery(id+"F4.wireOp",EDGE,"E30")])]}),makeQuery(id+"F8.opExtrude","SWEPT_FACE",FACE,{"disambiguationData":[OSD([sQuery(id+"F7.wireOp",EDGE,"E67")])]})]});
            fillet(context, id + "F14", {"entities" : qUnion([Q0, Q1, Q2, Q3, Q4, Q5]), "radius" : 3 * mm, "tangentPropagation" : true, "allowEdgeOverflow" : false});
        }
        {
            var Q0;
            Q0=makeQuery(id+"F1.opExtrude","CAP_EDGE",EDGE,{"disambiguationData":[OSD([sQuery(id+"F0.wireOp",EDGE,"E1.bottom")])],"isStart":false});
            fillet(context, id + "F15", {"entities" : qUnion([Q0]), "radius" : 2 * mm, "tangentPropagation" : true, "allowEdgeOverflow" : false});
        }
        {
            var Q0;
            {var subQ0=sQuery(id+"F0.wireOp",EDGE,"E21.filletArc");var subQ1=sQuery(id+"F0.wireOp",EDGE,"E7");var subQ2=sQuery(id+"F0.wireOp",EDGE,"E6");var subQ3=sQuery(id+"F0.wireOp",EDGE,"E5");var subQ4=sQuery(id+"F0.wireOp",EDGE,"E4");var subQ5=sQuery(id+"F0.wireOp",EDGE,"E22.filletArc");var subQ6=sQuery(id+"F0.wireOp",EDGE,"E1.bottom");var subQ7=sQuery(id+"F0.wireOp",EDGE,"E1.right");var subQ8=sQuery(id+"F0.wireOp",EDGE,"E1.top");var subQ9=sQuery(id+"F0.wireOp",EDGE,"E1.left");var subQ10=sQuery(id+"F0.wireOp",EDGE,"E23.filletArc");var subQ11=sQuery(id+"F0.wireOp",EDGE,"E24.filletArc");Q0=makeQuery(id+"F2.boolean.opBoolean","SPLIT",FACE,{"disambiguationData":[TD([makeQuery(id+"F1.opExtrude","SWEPT_FACE",FACE,{"disambiguationData":[OSD([subQ6])]})])],"derivedFrom":makeQuery(id+"F1.opExtrude","CAP_FACE",FACE,{"disambiguationData":[OSD([subQ6,subQ8,subQ9,subQ7,subQ4,subQ3,subQ2,subQ1,subQ0,subQ5,subQ10,subQ11])],"isStart":true})});}
            var sketch = newSketch(context, id + "F16", { "sketchPlane" : qUnion([Q0])});
            skLineSegment(sketch, "E79.0", {"start": v(80, -80) * mm, "end": v(80, 80) * mm});
            skArc(sketch, "E79.1", {"start": v(80, 80) * mm, "mid": v(77.07, 87.07) * mm, "end": v(70, 90) * mm});
            skLineSegment(sketch, "E79.2", {"start": v(-70, 90) * mm, "end": v(70, 90) * mm});
            skArc(sketch, "E79.3", {"start": v(-70, 90) * mm, "mid": v(-77.07, 87.07) * mm, "end": v(-80, 80) * mm});
            skLineSegment(sketch, "E79.4", {"start": v(-80, -80) * mm, "end": v(-80, 80) * mm});
            skArc(sketch, "E79.5", {"start": v(-80, -80) * mm, "mid": v(-77.07, -87.07) * mm, "end": v(-70, -90) * mm});
            skLineSegment(sketch, "E79.6", {"start": v(-70, -90) * mm, "end": v(70, -90) * mm});
            skArc(sketch, "E79.7", {"start": v(70, -90) * mm, "mid": v(77.07, -87.07) * mm, "end": v(80, -80) * mm});
            skArc(sketch, "E79.8", {"start": v(56.15, -48.18) * mm, "mid": v(58.99, -44.68) * mm, "end": v(60, -40.3) * mm});
            skLineSegment(sketch, "E79.9", {"start": v(60, 40.3) * mm, "end": v(60, -40.3) * mm});
            skArc(sketch, "E79.10", {"start": v(-56.15, -48.18) * mm, "mid": v(0, -67.5) * mm, "end": v(56.15, -48.18) * mm});
            skArc(sketch, "E79.11", {"start": v(-60, -40.3) * mm, "mid": v(-58.99, -44.68) * mm, "end": v(-56.15, -48.18) * mm});
            skLineSegment(sketch, "E79.12", {"start": v(-60, 40.3) * mm, "end": v(-60, -40.3) * mm});
            skArc(sketch, "E79.13", {"start": v(56.15, 48.18) * mm, "mid": v(0, 67.5) * mm, "end": v(-56.15, 48.18) * mm});
            skArc(sketch, "E79.14", {"start": v(-56.15, 48.18) * mm, "mid": v(-58.99, 44.68) * mm, "end": v(-60, 40.3) * mm});
            skArc(sketch, "E79.15", {"start": v(60, 40.3) * mm, "mid": v(58.99, 44.68) * mm, "end": v(56.15, 48.18) * mm});
            skCircle(sketch, "E80.0", {"center": v(60, 67.5) * mm, "radius": 4 * mm});
            skCircle(sketch, "E80.1", {"center": v(60, -67.5) * mm, "radius": 4 * mm});
            skCircle(sketch, "E80.2", {"center": v(-60, -67.5) * mm, "radius": 4 * mm});
            skCircle(sketch, "E80.3", {"center": v(-60, 67.5) * mm, "radius": 4 * mm});
            skArc(sketch, "E81", {"start": v(15, 119.76) * mm, "mid": v(0.25, 135) * mm, "end": v(-15, 120.26) * mm});
            skCircle(sketch, "E82", {"center": v(0, 120) * mm, "radius": 6 * mm});
            skLineSegment(sketch, "E83", {"start": v(-15, 120.26) * mm, "end": v(-15.3, 103.27) * mm});
            skLineSegment(sketch, "E84", {"start": v(-15.3, 103.27) * mm, "end": v(-27.46, 90) * mm});
            skLineSegment(sketch, "E85", {"start": v(15, 119.76) * mm, "end": v(15, 102.76) * mm});
            skLineSegment(sketch, "E86", {"start": v(15, 102.76) * mm, "end": v(27.7, 90) * mm});
            skLineSegment(sketch, "E87", {"start": v(0, 90) * mm, "end": v(0, 120) * mm, "construction": true});
            skLineSegment(sketch, "E88", {"start": v(-80, 0) * mm, "end": v(80, 0) * mm, "construction": true});
            skLineSegment(sketch, "E89.MirrorCS", {"start": v(0, -90) * mm, "end": v(0, -120) * mm, "construction": true});
            skArc(sketch, "E90.MirrorCS", {"start": v(15, -119.76) * mm, "mid": v(0.25, -135) * mm, "end": v(-15, -120.26) * mm});
            skLineSegment(sketch, "E91.MirrorCS", {"start": v(15, -102.76) * mm, "end": v(27.7, -90) * mm});
            skCircle(sketch, "E92.MirrorC", {"center": v(0, -120) * mm, "radius": 6 * mm});
            skLineSegment(sketch, "E93.MirrorCS", {"start": v(-15.3, -103.27) * mm, "end": v(-27.46, -90) * mm});
            skLineSegment(sketch, "E94.MirrorCS", {"start": v(-15, -120.26) * mm, "end": v(-15.3, -103.27) * mm});
            skLineSegment(sketch, "E95.MirrorCS", {"start": v(15, -119.76) * mm, "end": v(15, -102.76) * mm});
            skSolve(sketch);
        }
        {
            var Q0;
            Q0 = qSketchRegion(id + "F16", true);
            var Q1;
            Q1=makeQuery(id+"F2.opExtrude","CAP_FACE",FACE,{"disambiguationData":[OSD([sQuery(id+"F0.wireOp",EDGE,"E12"),sQuery(id+"F0.wireOp",EDGE,"E13"),sQuery(id+"F0.wireOp",EDGE,"E14"),sQuery(id+"F0.wireOp",EDGE,"E15"),sQuery(id+"F0.wireOp",EDGE,"E17.filletArc"),sQuery(id+"F0.wireOp",EDGE,"E18.filletArc"),sQuery(id+"F0.wireOp",EDGE,"E19.filletArc"),sQuery(id+"F0.wireOp",EDGE,"E20.filletArc"),sQuery(id+"F0.wireOp",EDGE,"E25.0"),sQuery(id+"F0.wireOp",EDGE,"E25.1"),sQuery(id+"F0.wireOp",EDGE,"E25.2"),sQuery(id+"F0.wireOp",EDGE,"E25.3"),sQuery(id+"F0.wireOp",EDGE,"E25.4"),sQuery(id+"F0.wireOp",EDGE,"E25.5"),sQuery(id+"F0.wireOp",EDGE,"E25.6"),sQuery(id+"F0.wireOp",EDGE,"E25.7")])],"isStart":false});
            extrude(context, id + "F17", {"entities" : qUnion([Q0]), "endBound" : BoundingType.UP_TO_SURFACE, "endBoundEntityFace" : qUnion([Q1]), "depth" : 25 * mm});
        }
    });
